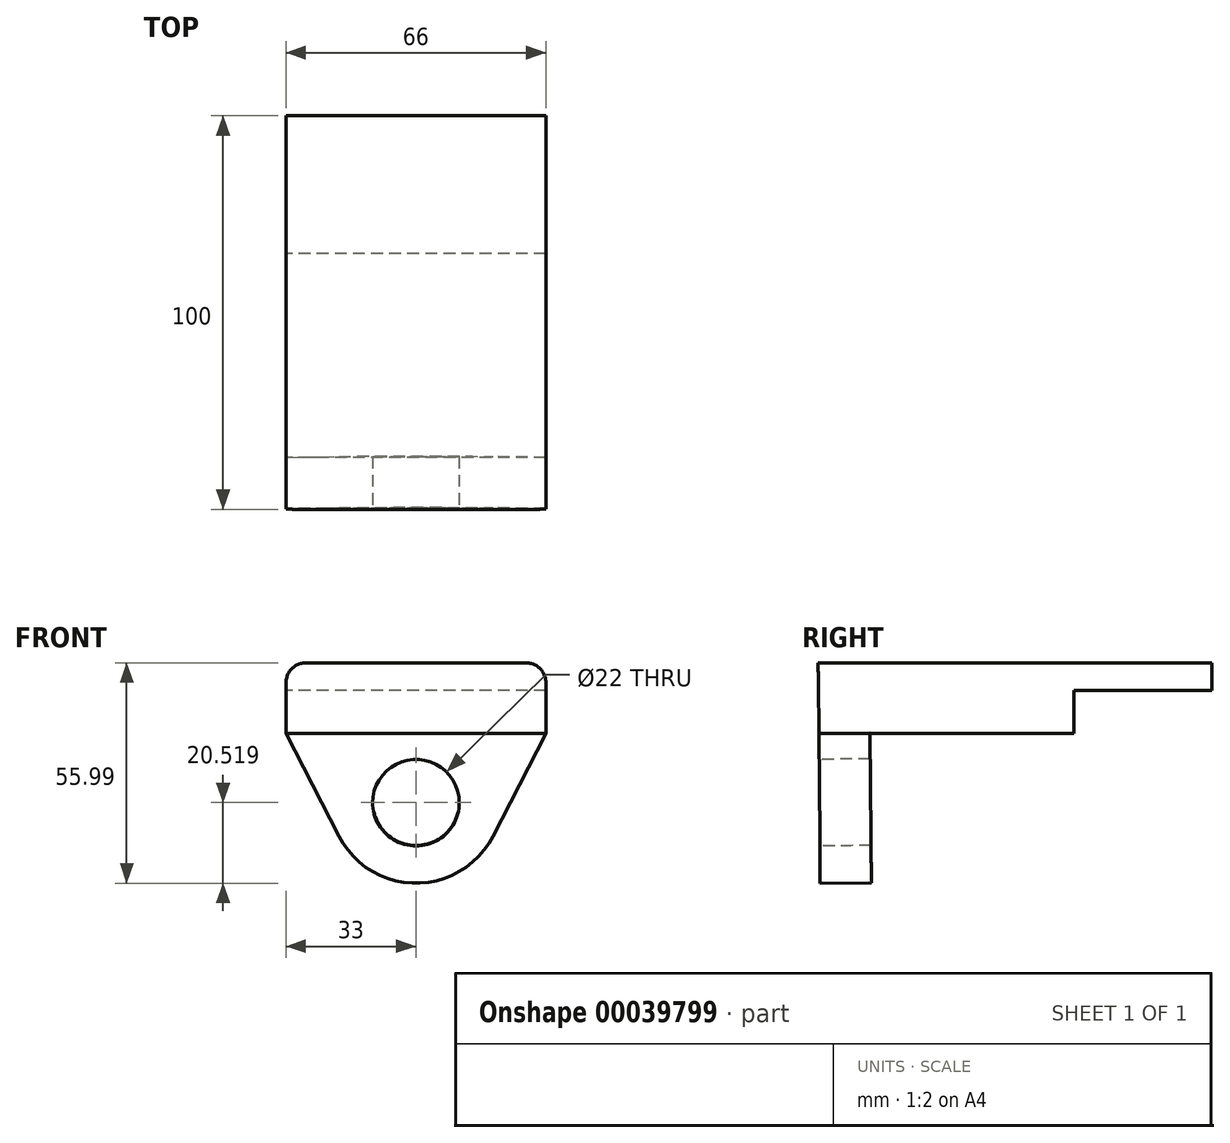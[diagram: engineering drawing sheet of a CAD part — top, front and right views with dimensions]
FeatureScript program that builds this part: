
annotation { "Feature Type Name" : "Feature", "Feature Type Description" : "" }
export const myFeature = defineFeature(function(context is Context, id is Id, definition is map)
    precondition{}
    {
        {
            var Q0;
            Q0=qCreatedBy(makeId("Right.planeOp"),FACE);
            var sketch = newSketch(context, id + "F0", { "sketchPlane" : qUnion([Q0])});
            skLineSegment(sketch, "E0", {"start": v(9.87, 1.94) * mm, "end": v(9.87, 12.93) * mm});
            skLineSegment(sketch, "E1", {"start": v(9.87, 12.93) * mm, "end": v(44.87, 12.93) * mm});
            skLineSegment(sketch, "E2", {"start": v(44.87, 12.93) * mm, "end": v(44.87, 19.93) * mm});
            skLineSegment(sketch, "E3", {"start": v(44.87, 19.93) * mm, "end": v(-55.13, 19.93) * mm});
            skLineSegment(sketch, "E4", {"start": v(9.87, 1.94) * mm, "end": v(-54.95, 1.94) * mm});
            skLineSegment(sketch, "E5", {"start": v(-54.95, 1.94) * mm, "end": v(-55.13, 19.93) * mm});
            skSolve(sketch);
        }
        {
            var Q0;
            Q0=makeQuery(id+"F0.imprint","IMPRINT",FACE,{"disambiguationData":[TD([[makeQuery(id+"F0.imprint","IMPRINT",EDGE,{"derivedFrom":sQuery(id+"F0.wireOp",EDGE,"E0")}),1.0]])]});
            extrude(context, id + "F1", {"entities" : qUnion([Q0]), "depth" : 66 * mm});
        }
        {
            var Q0;
            Q0=makeQuery(id+"F1.opExtrude","SWEPT_FACE",FACE,{"disambiguationData":[OSD([sQuery(id+"F0.wireOp",EDGE,"E5")])]});
            var sketch = newSketch(context, id + "F2", { "sketchPlane" : qUnion([Q0])});
            skArc(sketch, "E6", {"start": v(13.45, -23.63) * mm, "mid": v(33, -35.54) * mm, "end": v(52.55, -23.63) * mm});
            skLineSegment(sketch, "E7", {"start": v(0, 2.46) * mm, "end": v(66, 2.46) * mm});
            skLineSegment(sketch, "E8", {"start": v(0, 2.46) * mm, "end": v(13.45, -23.63) * mm});
            skLineSegment(sketch, "E9", {"start": v(66, 2.46) * mm, "end": v(52.55, -23.63) * mm});
            skSolve(sketch);
        }
        {
            var Q0;
            Q0=makeQuery(id+"F2.imprint","IMPRINT",FACE,{"disambiguationData":[TD([[makeQuery(id+"F2.imprint","IMPRINT",EDGE,{"derivedFrom":sQuery(id+"F2.wireOp",EDGE,"E6")}),1.0]])]});
            extrude(context, id + "F3", {"entities" : qUnion([Q0]), "oppositeDirection" : true, "depth" : 13 * mm});
        }
        {
            var Q0;
            Q0=makeQuery(id+"F3.opExtrude","CAP_FACE",FACE,{"disambiguationData":[OSD([sQuery(id+"F2.wireOp",EDGE,"E6"),sQuery(id+"F2.wireOp",EDGE,"E7"),sQuery(id+"F2.wireOp",EDGE,"E8"),sQuery(id+"F2.wireOp",EDGE,"E9")])],"isStart":true});
            var sketch = newSketch(context, id + "F4", { "sketchPlane" : qUnion([Q0])});
            skPoint(sketch, "E10", {"position": v(33, -15.08) * mm});
            skPoint(sketch, "E10.positionSnap0", {"position": v(33, -35.54) * mm});
            skSolve(sketch);
        }
        {
            var Q0;
            Q0=sQuery(id+"F4.wireOp",VERTEX,"E10");
            var Q1;
            Q1=makeQuery(id+"F3.opExtrude","SWEPT_BODY",BODY,{"disambiguationData":[OSD([sQuery(id+"F2.wireOp",EDGE,"E6"),sQuery(id+"F2.wireOp",EDGE,"E7"),sQuery(id+"F2.wireOp",EDGE,"E8"),sQuery(id+"F2.wireOp",EDGE,"E9")])]});
            hole(context, id + "F5", {"style" : HoleStyle.SIMPLE, "holeDiameter" : 22 * mm, "endStyle" : HoleEndStyle.THROUGH, "locations" : qUnion([Q0]), "scope" : qUnion([Q1])});
        }
        {
            var Q0;
            Q0=makeQuery(id+"F1.opExtrude","CAP_EDGE",EDGE,{"disambiguationData":[OSD([sQuery(id+"F0.wireOp",EDGE,"E3")])],"isStart":true});
            var Q1;
            Q1=makeQuery(id+"F1.opExtrude","CAP_EDGE",EDGE,{"disambiguationData":[OSD([sQuery(id+"F0.wireOp",EDGE,"E3")])],"isStart":false});
            fillet(context, id + "F6", {"entities" : qUnion([Q0, Q1]), "radius" : 5 * mm, "tangentPropagation" : true, "allowEdgeOverflow" : false});
        }
        {
            var Q0;
            Q0=makeQuery(id+"F1.opExtrude","CAP_FACE",FACE,{"disambiguationData":[OSD([sQuery(id+"F0.wireOp",EDGE,"E0"),sQuery(id+"F0.wireOp",EDGE,"E1"),sQuery(id+"F0.wireOp",EDGE,"E2"),sQuery(id+"F0.wireOp",EDGE,"E3"),sQuery(id+"F0.wireOp",EDGE,"E4"),sQuery(id+"F0.wireOp",EDGE,"E5")])],"isStart":false});
            var sketch = newSketch(context, id + "F7", { "sketchPlane" : qUnion([Q0])});
            skPoint(sketch, "E11", {"position": v(66.15, 0) * mm});
            skPoint(sketch, "E12", {"position": v(0, 0) * mm});
            skSolve(sketch);
        }
    });
